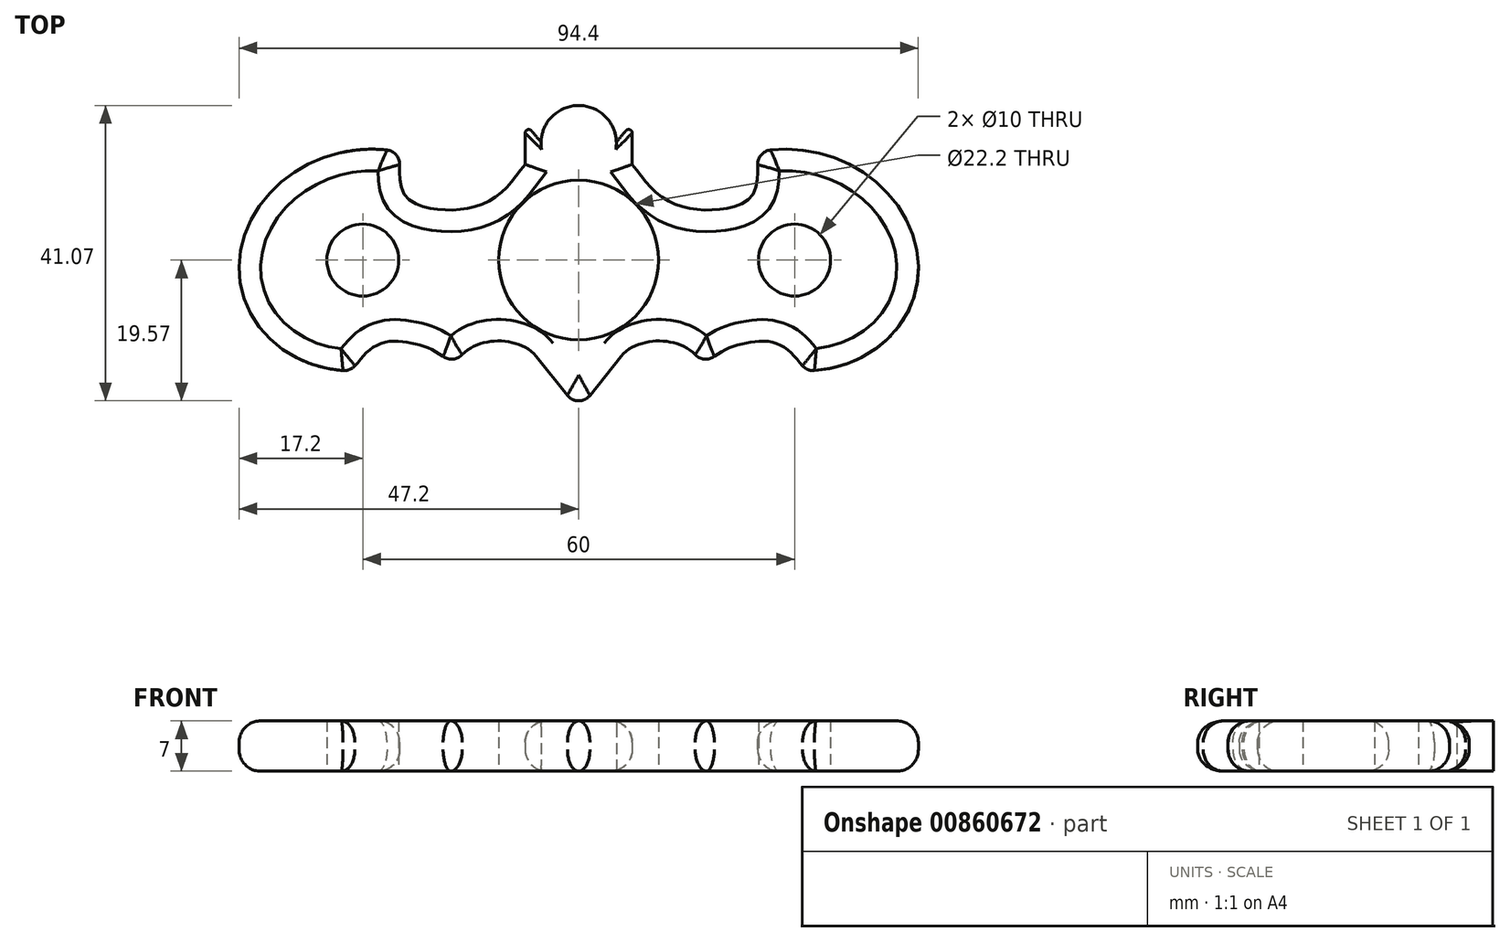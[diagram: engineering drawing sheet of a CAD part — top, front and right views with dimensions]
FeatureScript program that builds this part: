
annotation { "Feature Type Name" : "Feature", "Feature Type Description" : "" }
export const myFeature = defineFeature(function(context is Context, id is Id, definition is map)
    precondition{}
    {
        {
            var Q0;
            Q0=qCreatedBy(makeId("Top.planeOp"),FACE);
            var sketch = newSketch(context, id + "F0", { "sketchPlane" : qUnion([Q0])});
            skEllipticalArc(sketch, "E0", {});
            skFitSpline(sketch, "E1", {"points": [v(-24.85, 15) * mm, v(-24.85, 11.61) * mm, v(-23.78, 8.6) * mm, v(-17.44, 6.96) * mm, v(-11.04, 9.15) * mm, v(-7.44, 13.3) * mm], "startDerivative": vector(0, -24.66) * mm, "endDerivative": vector(13.5, 16.79) * mm});
            skFitSpline(sketch, "E2", {"points": [v(-31.78, -15.41) * mm, v(-29.04, -12.45) * mm, v(-26.55, -11.34) * mm, v(-24.61, -11.34) * mm, v(-21.01, -12.18) * mm, v(-17.14, -15.41) * mm], "startDerivative": vector(17.75, 17.63) * mm, "endDerivative": vector(5.44, -15.94) * mm});
            skFitSpline(sketch, "E3.MirrorCS", {"points": [v(24.85, 15) * mm, v(24.85, 11.61) * mm, v(23.78, 8.6) * mm, v(17.44, 6.96) * mm, v(11.04, 9.15) * mm, v(7.44, 13.3) * mm], "startDerivative": vector(0, -24.66) * mm, "endDerivative": vector(-13.5, 16.79) * mm});
            skEllipticalArc(sketch, "E4.MirrorCS", {});
            skFitSpline(sketch, "E5.MirrorCS", {"points": [v(31.78, -15.41) * mm, v(29.04, -12.45) * mm, v(26.55, -11.34) * mm, v(24.61, -11.34) * mm, v(21.01, -12.18) * mm, v(17.14, -15.41) * mm], "startDerivative": vector(-17.75, 17.63) * mm, "endDerivative": vector(-5.44, -15.94) * mm});
            skLineSegment(sketch, "E6", {"start": v(-7.44, 13.3) * mm, "end": v(-7.44, 19.02) * mm});
            skLineSegment(sketch, "E7", {"start": v(-7.44, 19.02) * mm, "end": v(-5.23, 16.4) * mm});
            skLineSegment(sketch, "E8.MirrorCS", {"start": v(7.44, 13.3) * mm, "end": v(7.44, 19.02) * mm});
            skLineSegment(sketch, "E9.MirrorCS", {"start": v(7.44, 19.02) * mm, "end": v(5.23, 16.4) * mm});
            skEllipticalArc(sketch, "E10", {});
            skCircle(sketch, "E11", {"center": v(0, 0) * mm, "radius": 11.1 * mm});
            skLineSegment(sketch, "E12", {"start": v(0, 28.67) * mm, "end": v(0, -30.63) * mm, "construction": true});
            skCircle(sketch, "E13", {"center": v(-30, 0) * mm, "radius": 5 * mm});
            skCircle(sketch, "E14.MirrorC", {"center": v(30, 0) * mm, "radius": 5 * mm});
            skEllipticalArc(sketch, "E15", {});
            skLineSegment(sketch, "E16", {"start": v(-5.9, -13.4) * mm, "end": v(0, -20.78) * mm});
            skEllipticalArc(sketch, "E17.MirrorCS", {});
            skLineSegment(sketch, "E18.MirrorCS", {"start": v(5.9, -13.4) * mm, "end": v(0, -20.78) * mm});
            const initialGuessF0  = {"E0": [-0.03, 0, 0.9585219013923777, 0.2850188845517807, 0.017367501887663866, 0.015236677044921694, 1.011625136897293, 4.353318233233013], "E4.MirrorCS": [0.03, 0, -0.9585219013923777, 0.2850188845517807, 0.017367501887663866, 0.015236677044921694, 1.9298670739465735, 5.271560170282293], "E10": [0, 0.016264285863821223, -0.9996158337324682, 0.02771614964858196, 0.005235664839974946, 0.005235670240196041, 3.197032052384431, 6.283185307179586], "E15": [-0.011143438518047333, -0.015412731650583747, -1, 0, 0.006, 0.004166618335717712, 3.6478288616114596, 0], "E17.MirrorCS": [0.011143438518047333, -0.015412731650583747, 1, 0, 0.006, 0.004166618335717712, 0, 2.6353564455681266]};
            skSetInitialGuess(sketch, initialGuessF0);
            skSolve(sketch);
        }
        {
            var Q0;
            Q0=makeQuery(id+"F0.imprint","IMPRINT",FACE,{"disambiguationData":[TD([[makeQuery(id+"F0.imprint","IMPRINT",EDGE,{"derivedFrom":sQuery(id+"F0.wireOp",EDGE,"E0")}),1.0]])]});
            extrude(context, id + "F1", {"entities" : qUnion([Q0]), "depth" : 7 * mm, "offsetDistance" : 25 * mm});
        }
        {
            var Q0;
            Q0=makeQuery(id+"F1.opExtrude","CAP_EDGE",EDGE,{"disambiguationData":[OSD([sQuery(id+"F0.wireOp",EDGE,"E15")])],"isStart":false});
            var Q1;
            Q1=makeQuery(id+"F1.opExtrude","CAP_EDGE",EDGE,{"disambiguationData":[OSD([sQuery(id+"F0.wireOp",EDGE,"E17.MirrorCS")])],"isStart":false});
            var Q2;
            Q2=makeQuery(id+"F1.opExtrude","CAP_EDGE",EDGE,{"disambiguationData":[OSD([sQuery(id+"F0.wireOp",EDGE,"E5.MirrorCS")])],"isStart":false});
            var Q3;
            Q3=makeQuery(id+"F1.opExtrude","CAP_EDGE",EDGE,{"disambiguationData":[OSD([sQuery(id+"F0.wireOp",EDGE,"E4.MirrorCS")])],"isStart":false});
            var Q4;
            Q4=makeQuery(id+"F1.opExtrude","CAP_EDGE",EDGE,{"disambiguationData":[OSD([sQuery(id+"F0.wireOp",EDGE,"E3.MirrorCS")])],"isStart":false});
            var Q5;
            Q5=makeQuery(id+"F1.opExtrude","CAP_EDGE",EDGE,{"disambiguationData":[OSD([sQuery(id+"F0.wireOp",EDGE,"E8.MirrorCS")])],"isStart":false});
            var Q6;
            Q6=makeQuery(id+"F1.opExtrude","CAP_EDGE",EDGE,{"disambiguationData":[OSD([sQuery(id+"F0.wireOp",EDGE,"E6")])],"isStart":false});
            var Q7;
            Q7=makeQuery(id+"F1.opExtrude","CAP_EDGE",EDGE,{"disambiguationData":[OSD([sQuery(id+"F0.wireOp",EDGE,"E1")])],"isStart":false});
            var Q8;
            Q8=makeQuery(id+"F1.opExtrude","CAP_EDGE",EDGE,{"disambiguationData":[OSD([sQuery(id+"F0.wireOp",EDGE,"E2")])],"isStart":false});
            var Q9;
            Q9=makeQuery(id+"F1.opExtrude","CAP_EDGE",EDGE,{"disambiguationData":[OSD([sQuery(id+"F0.wireOp",EDGE,"E0")])],"isStart":false});
            var Q10;
            Q10=makeQuery(id+"F1.opExtrude","CAP_EDGE",EDGE,{"disambiguationData":[OSD([sQuery(id+"F0.wireOp",EDGE,"E18.MirrorCS")])],"isStart":false});
            var Q11;
            Q11=makeQuery(id+"F1.opExtrude","CAP_EDGE",EDGE,{"disambiguationData":[OSD([sQuery(id+"F0.wireOp",EDGE,"E16")])],"isStart":false});
            var Q12;
            Q12=makeQuery(id+"F1.opExtrude","CAP_EDGE",EDGE,{"disambiguationData":[OSD([sQuery(id+"F0.wireOp",EDGE,"E0")])],"isStart":true});
            var Q13;
            Q13=makeQuery(id+"F1.opExtrude","CAP_EDGE",EDGE,{"disambiguationData":[OSD([sQuery(id+"F0.wireOp",EDGE,"E2")])],"isStart":true});
            var Q14;
            Q14=makeQuery(id+"F1.opExtrude","CAP_EDGE",EDGE,{"disambiguationData":[OSD([sQuery(id+"F0.wireOp",EDGE,"E15")])],"isStart":true});
            var Q15;
            Q15=makeQuery(id+"F1.opExtrude","CAP_EDGE",EDGE,{"disambiguationData":[OSD([sQuery(id+"F0.wireOp",EDGE,"E17.MirrorCS")])],"isStart":true});
            var Q16;
            Q16=makeQuery(id+"F1.opExtrude","CAP_EDGE",EDGE,{"disambiguationData":[OSD([sQuery(id+"F0.wireOp",EDGE,"E5.MirrorCS")])],"isStart":true});
            var Q17;
            Q17=makeQuery(id+"F1.opExtrude","CAP_EDGE",EDGE,{"disambiguationData":[OSD([sQuery(id+"F0.wireOp",EDGE,"E4.MirrorCS")])],"isStart":true});
            var Q18;
            Q18=makeQuery(id+"F1.opExtrude","CAP_EDGE",EDGE,{"disambiguationData":[OSD([sQuery(id+"F0.wireOp",EDGE,"E3.MirrorCS")])],"isStart":true});
            var Q19;
            Q19=makeQuery(id+"F1.opExtrude","CAP_EDGE",EDGE,{"disambiguationData":[OSD([sQuery(id+"F0.wireOp",EDGE,"E8.MirrorCS")])],"isStart":true});
            var Q20;
            Q20=makeQuery(id+"F1.opExtrude","CAP_EDGE",EDGE,{"disambiguationData":[OSD([sQuery(id+"F0.wireOp",EDGE,"E6")])],"isStart":true});
            var Q21;
            Q21=makeQuery(id+"F1.opExtrude","CAP_EDGE",EDGE,{"disambiguationData":[OSD([sQuery(id+"F0.wireOp",EDGE,"E1")])],"isStart":true});
            fillet(context, id + "F2", {"entities" : qUnion([Q0, Q1, Q2, Q3, Q4, Q5, Q6, Q7, Q8, Q9, Q10, Q11, Q12, Q13, Q14, Q15, Q16, Q17, Q18, Q19, Q20, Q21]), "radius" : 3 * mm, "tangentPropagation" : true, "allowEdgeOverflow" : false});
        }
        {
            var Q0;
            Q0=makeQuery(id+"F2.opFillet","BLEND_EDGE",EDGE,{"blendedFrom":[makeQuery(id+"F1.opExtrude","CAP_EDGE",EDGE,{"disambiguationData":[OSD([sQuery(id+"F0.wireOp",EDGE,"E16")])],"isStart":true}),makeQuery(id+"F1.opExtrude","CAP_EDGE",EDGE,{"disambiguationData":[OSD([sQuery(id+"F0.wireOp",EDGE,"E18.MirrorCS")])],"isStart":true})],"blendedInto":[]});
            var Q1;
            Q1=makeQuery(id+"F2.opFillet","BLEND_EDGE",EDGE,{"blendedFrom":[makeQuery(id+"F1.opExtrude","CAP_EDGE",EDGE,{"disambiguationData":[OSD([sQuery(id+"F0.wireOp",EDGE,"E2")])],"isStart":false}),makeQuery(id+"F1.opExtrude","CAP_EDGE",EDGE,{"disambiguationData":[OSD([sQuery(id+"F0.wireOp",EDGE,"E15")])],"isStart":false})],"blendedInto":[]});
            var Q2;
            Q2=makeQuery(id+"F2.opFillet","BLEND_EDGE",EDGE,{"blendedFrom":[makeQuery(id+"F1.opExtrude","CAP_EDGE",EDGE,{"disambiguationData":[OSD([sQuery(id+"F0.wireOp",EDGE,"E0")])],"isStart":false}),makeQuery(id+"F1.opExtrude","CAP_EDGE",EDGE,{"disambiguationData":[OSD([sQuery(id+"F0.wireOp",EDGE,"E2")])],"isStart":false})],"blendedInto":[]});
            var Q3;
            Q3=makeQuery(id+"F2.opFillet","BLEND_EDGE",EDGE,{"blendedFrom":[makeQuery(id+"F1.opExtrude","CAP_EDGE",EDGE,{"disambiguationData":[OSD([sQuery(id+"F0.wireOp",EDGE,"E5.MirrorCS")])],"isStart":false}),makeQuery(id+"F1.opExtrude","CAP_EDGE",EDGE,{"disambiguationData":[OSD([sQuery(id+"F0.wireOp",EDGE,"E17.MirrorCS")])],"isStart":false})],"blendedInto":[]});
            var Q4;
            Q4=makeQuery(id+"F2.opFillet","BLEND_EDGE",EDGE,{"blendedFrom":[makeQuery(id+"F1.opExtrude","CAP_EDGE",EDGE,{"disambiguationData":[OSD([sQuery(id+"F0.wireOp",EDGE,"E4.MirrorCS")])],"isStart":false}),makeQuery(id+"F1.opExtrude","CAP_EDGE",EDGE,{"disambiguationData":[OSD([sQuery(id+"F0.wireOp",EDGE,"E5.MirrorCS")])],"isStart":false})],"blendedInto":[]});
            var Q5;
            Q5=makeQuery(id+"F2.opFillet","BLEND_EDGE",EDGE,{"blendedFrom":[makeQuery(id+"F1.opExtrude","CAP_EDGE",EDGE,{"disambiguationData":[OSD([sQuery(id+"F0.wireOp",EDGE,"E3.MirrorCS")])],"isStart":true}),makeQuery(id+"F1.opExtrude","CAP_EDGE",EDGE,{"disambiguationData":[OSD([sQuery(id+"F0.wireOp",EDGE,"E4.MirrorCS")])],"isStart":true})],"blendedInto":[]});
            var Q6;
            Q6=makeQuery(id+"F2.opFillet","BLEND_EDGE",EDGE,{"blendedFrom":[makeQuery(id+"F1.opExtrude","CAP_EDGE",EDGE,{"disambiguationData":[OSD([sQuery(id+"F0.wireOp",EDGE,"E0")])],"isStart":true}),makeQuery(id+"F1.opExtrude","CAP_EDGE",EDGE,{"disambiguationData":[OSD([sQuery(id+"F0.wireOp",EDGE,"E1")])],"isStart":true})],"blendedInto":[]});
            fillet(context, id + "F3", {"entities" : qUnion([Q0, Q1, Q2, Q3, Q4, Q5, Q6]), "radius" : 2 * mm, "tangentPropagation" : true, "allowEdgeOverflow" : false});
        }
        {
            var Q0;
            Q0=makeQuery(id+"F2.opFillet","BLEND_EDGE",EDGE,{"blendedFrom":[makeQuery(id+"F1.opExtrude","CAP_EDGE",EDGE,{"disambiguationData":[OSD([sQuery(id+"F0.wireOp",EDGE,"E8.MirrorCS")])],"isStart":false}),makeQuery(id+"F1.opExtrude","SWEPT_FACE",FACE,{"disambiguationData":[OSD([sQuery(id+"F0.wireOp",EDGE,"E9.MirrorCS")])]})],"blendedInto":[makeQuery(id+"F1.opExtrude","SWEPT_FACE",FACE,{"disambiguationData":[OSD([sQuery(id+"F0.wireOp",EDGE,"E9.MirrorCS")])]})]});
            var Q1;
            Q1=makeQuery(id+"F2.opFillet","BLEND_EDGE",EDGE,{"blendedFrom":[makeQuery(id+"F1.opExtrude","CAP_EDGE",EDGE,{"disambiguationData":[OSD([sQuery(id+"F0.wireOp",EDGE,"E6")])],"isStart":false}),makeQuery(id+"F1.opExtrude","SWEPT_FACE",FACE,{"disambiguationData":[OSD([sQuery(id+"F0.wireOp",EDGE,"E7")])]})],"blendedInto":[makeQuery(id+"F1.opExtrude","SWEPT_FACE",FACE,{"disambiguationData":[OSD([sQuery(id+"F0.wireOp",EDGE,"E7")])]})]});
            fillet(context, id + "F4", {"entities" : qUnion([Q0, Q1]), "radius" : 0.5 * mm, "tangentPropagation" : true, "allowEdgeOverflow" : false});
        }
    });
